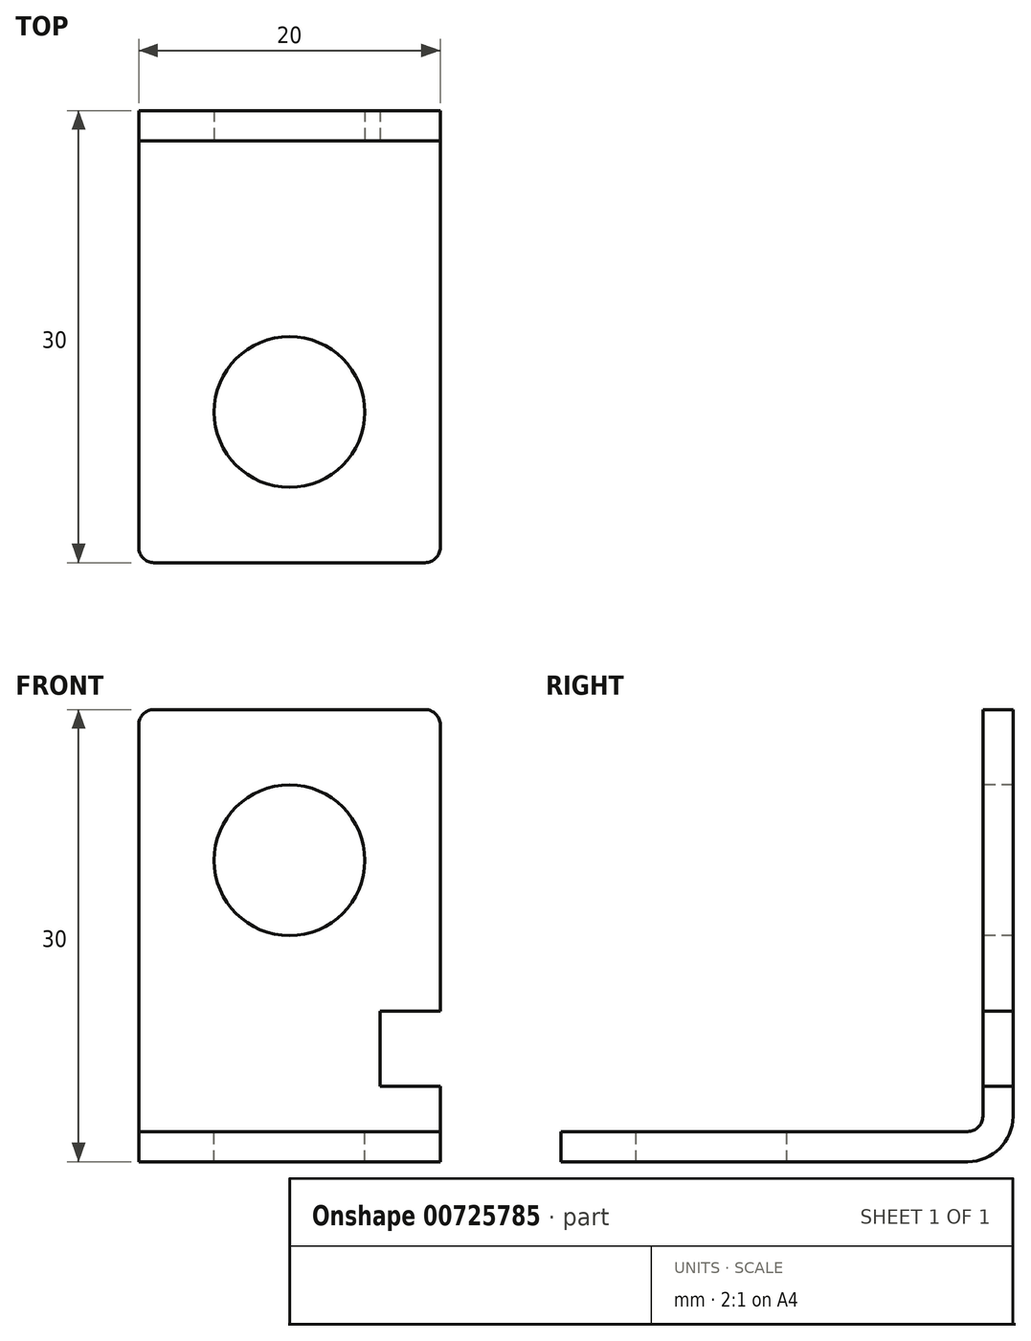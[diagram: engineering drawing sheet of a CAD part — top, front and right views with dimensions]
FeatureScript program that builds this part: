
annotation { "Feature Type Name" : "Feature", "Feature Type Description" : "" }
export const myFeature = defineFeature(function(context is Context, id is Id, definition is map)
    precondition{}
    {
        {
            var Q0;
            Q0=qCreatedBy(makeId("Right.planeOp"),FACE);
            var sketch = newSketch(context, id + "F0", { "sketchPlane" : qUnion([Q0])});
            skLineSegment(sketch, "E0.bottom", {"start": v(15, -15) * mm, "end": v(-15, -15) * mm});
            skLineSegment(sketch, "E0.top", {"start": v(15, 15) * mm, "end": v(-15, 15) * mm});
            skLineSegment(sketch, "E0.left", {"start": v(15, -15) * mm, "end": v(15, 15) * mm});
            skLineSegment(sketch, "E0.right", {"start": v(-15, -15) * mm, "end": v(-15, 15) * mm});
            skPoint(sketch, "E0.middle", {"position": v(0, 0) * mm});
            skSolve(sketch);
        }
        {
            var Q0;
            Q0 = qSketchRegion(id + "F0", true);
            extrude(context, id + "F1", {"entities" : qUnion([Q0]), "depth" : 20 * mm, "offsetDistance" : 25 * mm});
        }
        {
            var Q0;
            Q0=makeQuery(id+"F1.opExtrude","SWEPT_EDGE",EDGE,{"disambiguationData":[OSD([sQuery(id+"F0.wireOp",EDGE,"E0.bottom"),sQuery(id+"F0.wireOp",EDGE,"E0.left")])]});
            fillet(context, id + "F2", {"entities" : qUnion([Q0]), "radius" : 3 * mm, "tangentPropagation" : true, "allowEdgeOverflow" : false});
        }
        {
            var Q0;
            Q0=makeQuery(id+"F1.opExtrude","CAP_FACE",FACE,{"disambiguationData":[OSD([sQuery(id+"F0.wireOp",EDGE,"E0.bottom"),sQuery(id+"F0.wireOp",EDGE,"E0.top"),sQuery(id+"F0.wireOp",EDGE,"E0.left"),sQuery(id+"F0.wireOp",EDGE,"E0.right")])],"isStart":false});
            var sketch = newSketch(context, id + "F3", { "sketchPlane" : qUnion([Q0])});
            skLineSegment(sketch, "E1", {"start": v(-15, -13) * mm, "end": v(12, -13) * mm});
            skLineSegment(sketch, "E2", {"start": v(13, -12) * mm, "end": v(13, 15) * mm});
            skPoint(sketch, "E3.visualSharp", {"position": v(13, -13) * mm});
            skArc(sketch, "E3.filletArc", {"start": v(12, -13) * mm, "mid": v(12.7, -12.7) * mm, "end": v(13, -12) * mm});
            skSolve(sketch);
        }
        {
            var Q0;
            {var subQ4=sQuery(id+"F3.wireOp",EDGE,"E1");Q0=makeQuery(id+"F3.imprint","IMPRINT",FACE,{"disambiguationData":[TD([[makeQuery(id+"F3.imprint","IMPRINT",EDGE,{"derivedFrom":subQ4}),1.0]])]});}
            extrude(context, id + "F4", {"entities" : qUnion([Q0]), "operationType" : NewBodyOperationType.REMOVE, "endBound" : BoundingType.THROUGH_ALL, "oppositeDirection" : true, "depth" : 25 * mm, "offsetDistance" : 25 * mm});
        }
        {
            var Q0;
            Q0=makeQuery(id+"F1.opExtrude","CAP_EDGE",EDGE,{"disambiguationData":[OSD([sQuery(id+"F0.wireOp",EDGE,"E0.right")])],"isStart":false});
            var Q1;
            Q1=makeQuery(id+"F1.opExtrude","CAP_EDGE",EDGE,{"disambiguationData":[OSD([sQuery(id+"F0.wireOp",EDGE,"E0.top")])],"isStart":false});
            var Q2;
            Q2=makeQuery(id+"F1.opExtrude","CAP_EDGE",EDGE,{"disambiguationData":[OSD([sQuery(id+"F0.wireOp",EDGE,"E0.top")])],"isStart":true});
            var Q3;
            Q3=makeQuery(id+"F1.opExtrude","CAP_EDGE",EDGE,{"disambiguationData":[OSD([sQuery(id+"F0.wireOp",EDGE,"E0.right")])],"isStart":true});
            fillet(context, id + "F5", {"entities" : qUnion([Q0, Q1, Q2, Q3]), "radius" : 1 * mm, "tangentPropagation" : true, "allowEdgeOverflow" : false});
        }
        {
            var Q0;
            Q0=makeQuery(id+"F4.boolean.opBoolean","COPY",FACE,{"derivedFrom":makeQuery(id+"F4.opExtrude","SWEPT_FACE",FACE,{"disambiguationData":[OSD([sQuery(id+"F3.wireOp",EDGE,"E1")])]})});
            var sketch = newSketch(context, id + "F6", { "sketchPlane" : qUnion([Q0])});
            skCircle(sketch, "E4", {"center": v(10, -5) * mm, "radius": 5 * mm});
            skSolve(sketch);
        }
        {
            var Q0;
            Q0=makeQuery(id+"F6.imprint","IMPRINT",FACE,{"disambiguationData":[TD([[makeQuery(id+"F6.imprint","IMPRINT",EDGE,{"derivedFrom":sQuery(id+"F6.wireOp",EDGE,"E4")}),1.0]])]});
            extrude(context, id + "F7", {"entities" : qUnion([Q0]), "operationType" : NewBodyOperationType.REMOVE, "endBound" : BoundingType.THROUGH_ALL, "oppositeDirection" : true, "depth" : 25 * mm, "offsetDistance" : 25 * mm});
        }
        {
            var Q0;
            Q0=makeQuery(id+"F4.boolean.opBoolean","COPY",FACE,{"derivedFrom":makeQuery(id+"F4.opExtrude","SWEPT_FACE",FACE,{"disambiguationData":[OSD([sQuery(id+"F3.wireOp",EDGE,"E2")])]})});
            var sketch = newSketch(context, id + "F8", { "sketchPlane" : qUnion([Q0])});
            skCircle(sketch, "E5", {"center": v(10, 5) * mm, "radius": 5 * mm});
            skSolve(sketch);
        }
        {
            var Q0;
            Q0=makeQuery(id+"F8.imprint","IMPRINT",FACE,{"disambiguationData":[TD([[makeQuery(id+"F8.imprint","IMPRINT",EDGE,{"derivedFrom":sQuery(id+"F8.wireOp",EDGE,"E5")}),1.0]])]});
            extrude(context, id + "F9", {"entities" : qUnion([Q0]), "operationType" : NewBodyOperationType.REMOVE, "endBound" : BoundingType.THROUGH_ALL, "oppositeDirection" : true, "depth" : 25 * mm, "offsetDistance" : 25 * mm});
        }
        {
            var Q0;
            Q0=makeQuery(id+"F4.boolean.opBoolean","COPY",FACE,{"derivedFrom":makeQuery(id+"F4.opExtrude","SWEPT_FACE",FACE,{"disambiguationData":[OSD([sQuery(id+"F3.wireOp",EDGE,"E2")])]})});
            var sketch = newSketch(context, id + "F10", { "sketchPlane" : qUnion([Q0])});
            skLineSegment(sketch, "E6.bottom", {"start": v(20, -5) * mm, "end": v(16, -5) * mm});
            skLineSegment(sketch, "E6.top", {"start": v(20, -10) * mm, "end": v(16, -10) * mm});
            skLineSegment(sketch, "E6.left", {"start": v(20, -5) * mm, "end": v(20, -10) * mm});
            skLineSegment(sketch, "E6.right", {"start": v(16, -5) * mm, "end": v(16, -10) * mm});
            skSolve(sketch);
        }
        {
            var Q0;
            Q0=makeQuery(id+"F10.imprint","IMPRINT",FACE,{"disambiguationData":[TD([[makeQuery(id+"F10.imprint","IMPRINT",EDGE,{"derivedFrom":sQuery(id+"F10.wireOp",EDGE,"E6.bottom")}),1.0]])]});
            extrude(context, id + "F11", {"entities" : qUnion([Q0]), "operationType" : NewBodyOperationType.REMOVE, "endBound" : BoundingType.THROUGH_ALL, "oppositeDirection" : true, "depth" : 25 * mm, "offsetDistance" : 25 * mm});
        }
    });
